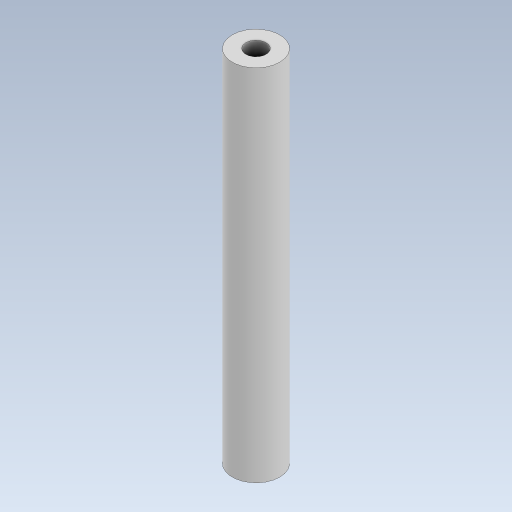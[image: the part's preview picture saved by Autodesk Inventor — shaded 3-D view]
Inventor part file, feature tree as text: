
AUTODESK INVENTOR PART (.ipt)
format: ipt  version: 2023.5 (Build 275446000, 446)  size: 81,408 bytes
history: native  units: mm
features: extrude x1, sketch x1
ambient origin geometry x8: Origin, YZ Plane, XZ Plane, XY Plane, X Axis, Y Axis, Z Axis, Center Point
bodies: Solid1 (feature_tree)
feature tree (2):
  extrude  "Extrusion1"  Depth=53.0mm
  sketch  "Sketch1"  dims[d0=7.0mm d1=3.0mm d2=53.0mm d3=0.0mm]
